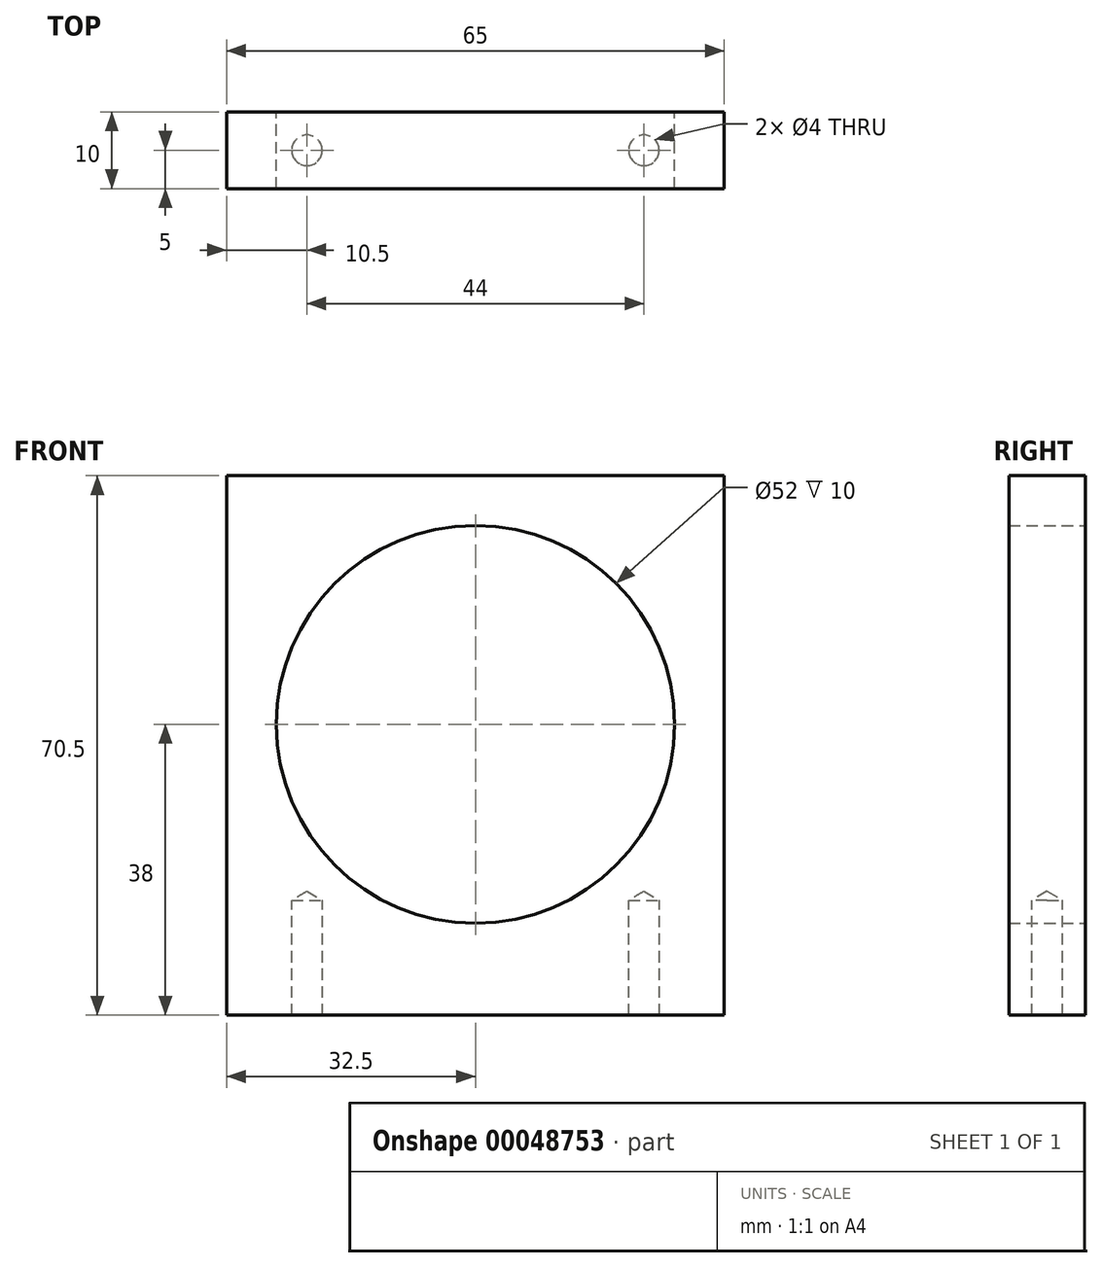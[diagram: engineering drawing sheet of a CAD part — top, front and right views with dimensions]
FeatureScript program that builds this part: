
annotation { "Feature Type Name" : "Feature", "Feature Type Description" : "" }
export const myFeature = defineFeature(function(context is Context, id is Id, definition is map)
    precondition{}
    {
        {
            var Q0;
            Q0=qCreatedBy(makeId("Front.planeOp"),FACE);
            var sketch = newSketch(context, id + "F0", { "sketchPlane" : qUnion([Q0])});
            skLineSegment(sketch, "E0.bottom", {"start": v(32.5, -38) * mm, "end": v(-32.5, -38) * mm});
            skLineSegment(sketch, "E0.top", {"start": v(32.5, 32.5) * mm, "end": v(-32.5, 32.5) * mm});
            skLineSegment(sketch, "E0.left", {"start": v(32.5, -38) * mm, "end": v(32.5, 32.5) * mm});
            skLineSegment(sketch, "E0.right", {"start": v(-32.5, -38) * mm, "end": v(-32.5, 32.5) * mm});
            skPoint(sketch, "E0.middle", {"position": v(0, 0) * mm});
            skCircle(sketch, "E1", {"center": v(0, 0) * mm, "radius": 26 * mm});
            skSolve(sketch);
        }
        {
            var Q0;
            Q0=makeQuery(id+"F0.imprint","IMPRINT",FACE,{"disambiguationData":[TD([[makeQuery(id+"F0.imprint","IMPRINT",EDGE,{"derivedFrom":sQuery(id+"F0.wireOp",EDGE,"E0.bottom")}),-1.0]])]});
            extrude(context, id + "F1", {"entities" : qUnion([Q0]), "depth" : 10 * mm, "symmetric" : true});
        }
        {
            var Q0;
            Q0=makeQuery(id+"F1.opExtrude","SWEPT_FACE",FACE,{"disambiguationData":[OSD([sQuery(id+"F0.wireOp",EDGE,"E0.bottom")])]});
            var sketch = newSketch(context, id + "F2", { "sketchPlane" : qUnion([Q0])});
            skPoint(sketch, "E2", {"position": v(-22, 0) * mm});
            skPoint(sketch, "E3.MirrorP", {"position": v(22, 0) * mm});
            skSolve(sketch);
        }
        {
            var Q0;
            Q0=sQuery(id+"F2.wireOp",VERTEX,"E2");
            var Q1;
            Q1=sQuery(id+"F2.wireOp",VERTEX,"E3.MirrorP");
            var Q2;
            Q2=makeQuery(id+"F1.opExtrude","SWEPT_BODY",BODY,{"disambiguationData":[OSD([sQuery(id+"F0.wireOp",EDGE,"E0.bottom"),sQuery(id+"F0.wireOp",EDGE,"E0.top"),sQuery(id+"F0.wireOp",EDGE,"E0.left"),sQuery(id+"F0.wireOp",EDGE,"E0.right"),sQuery(id+"F0.wireOp",EDGE,"E1")])]});
            hole(context, id + "F3", {"style" : HoleStyle.SIMPLE, "endStyle" : HoleEndStyle.BLIND, "standardTappedOrClearance" : lookupTablePath({ "standard" : "ISO", "engagement" : "75%", "pitch" : "1 mm", "size" : "M5", "type" : "Tapped" }), "standardBlindInLast" : lookupTablePath({ "standard" : "ISO", "engagement" : "75%", "pitch" : "1 mm", "size" : "M5", "type" : "Tapped" }), "holeDiameter" : 4 * mm, "showTappedDepth" : true, "holeDepth" : 15 * mm, "tappedDepth" : 12 * mm, "tapClearance" : 3, "locations" : qUnion([Q0, Q1]), "scope" : qUnion([Q2]), "startStyle" : HoleStartStyle.PART});
        }
    });
